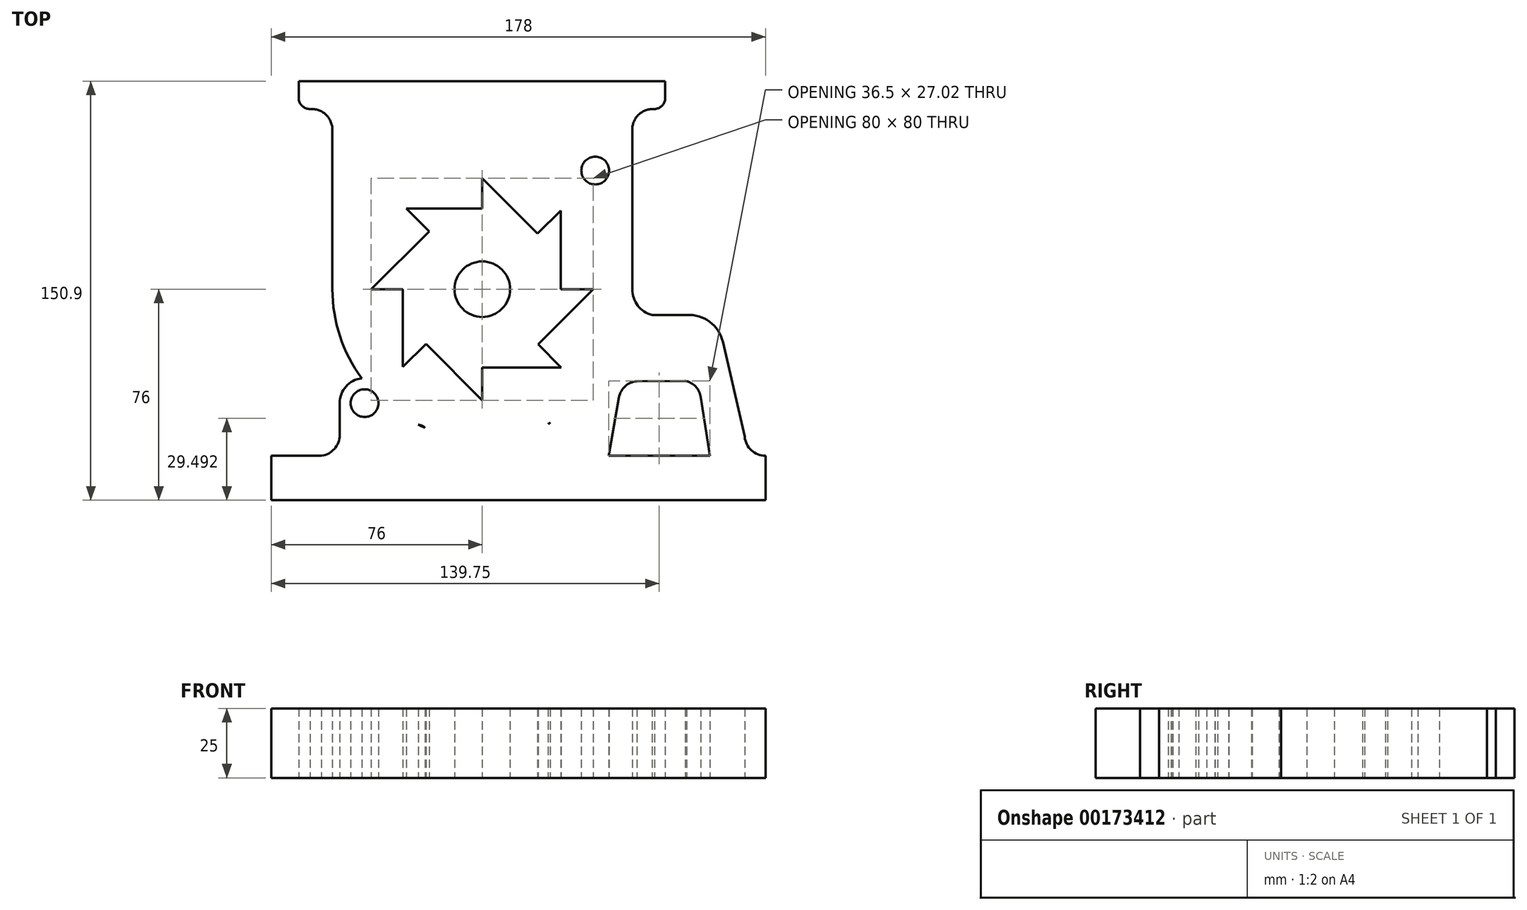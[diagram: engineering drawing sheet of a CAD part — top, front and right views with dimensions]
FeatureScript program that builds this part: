
annotation { "Feature Type Name" : "Feature", "Feature Type Description" : "" }
export const myFeature = defineFeature(function(context is Context, id is Id, definition is map)
    precondition{}
    {
        {
            var Q0;
            Q0=qCreatedBy(makeId("Top.planeOp"),FACE);
            var sketch = newSketch(context, id + "F0", { "sketchPlane" : qUnion([Q0])});
            skCircle(sketch, "E0", {"center": v(0, 0) * mm, "radius": 10 * mm});
            skCircle(sketch, "E1", {"center": v(0, 0) * mm, "radius": 45 * mm});
            skArc(sketch, "E2", {"start": v(-33.49, -42.36) * mm, "mid": v(38.34, -38.02) * mm, "end": v(42.08, 33.84) * mm});
            skLineSegment(sketch, "E3", {"start": v(0, 10) * mm, "end": v(0, 40) * mm});
            skLineSegment(sketch, "E4", {"start": v(10, 0) * mm, "end": v(40, 0) * mm});
            skLineSegment(sketch, "E5", {"start": v(0, -10) * mm, "end": v(0, -40) * mm});
            skLineSegment(sketch, "E6", {"start": v(-10, 0) * mm, "end": v(-40, 0) * mm});
            skLineSegment(sketch, "E7", {"start": v(7, 7.14) * mm, "end": v(28.22, 28.35) * mm});
            skLineSegment(sketch, "E8", {"start": v(7.18, -6.96) * mm, "end": v(28.4, -28.17) * mm});
            skLineSegment(sketch, "E9", {"start": v(-7.37, -6.76) * mm, "end": v(-28.58, -27.98) * mm});
            skLineSegment(sketch, "E10", {"start": v(-6.19, 7.86) * mm, "end": v(-27.4, 29.07) * mm});
            skLineSegment(sketch, "E11", {"start": v(-27.4, 29.07) * mm, "end": v(0, 29.07) * mm});
            skLineSegment(sketch, "E12", {"start": v(28.22, 28.35) * mm, "end": v(28.22, 0) * mm});
            skLineSegment(sketch, "E13", {"start": v(28.4, -28.17) * mm, "end": v(0, -28.17) * mm});
            skPoint(sketch, "E13.endSnap0", {"position": v(0, -25) * mm});
            skLineSegment(sketch, "E14", {"start": v(-28.58, -27.98) * mm, "end": v(-28.58, 0) * mm});
            skLineSegment(sketch, "E15", {"start": v(-40, 0) * mm, "end": v(-19.16, 20.84) * mm});
            skLineSegment(sketch, "E16", {"start": v(0, 40) * mm, "end": v(19.94, 20.06) * mm});
            skLineSegment(sketch, "E17", {"start": v(40, 0) * mm, "end": v(20.11, -19.89) * mm});
            skLineSegment(sketch, "E18", {"start": v(0, -40) * mm, "end": v(-20.3, -19.7) * mm});
            skLineSegment(sketch, "E19", {"start": v(-54, 0) * mm, "end": v(-54, 57.42) * mm});
            skLineSegment(sketch, "E20", {"start": v(54, 0) * mm, "end": v(54, 57.42) * mm});
            skArc(sketch, "E21", {"start": v(62.07, 64.9) * mm, "mid": v(56.4, 62.93) * mm, "end": v(54, 57.42) * mm});
            skArc(sketch, "E22", {"start": v(-54, 57.42) * mm, "mid": v(-56.4, 62.93) * mm, "end": v(-62.07, 64.9) * mm});
            skArc(sketch, "E23", {"start": v(-66.06, 68.05) * mm, "mid": v(-64.63, 65.76) * mm, "end": v(-62.07, 64.9) * mm});
            skArc(sketch, "E24", {"start": v(62.07, 64.9) * mm, "mid": v(64.5, 65.83) * mm, "end": v(65.84, 68.05) * mm});
            skLineSegment(sketch, "E25", {"start": v(65.84, 68.05) * mm, "end": v(65.84, 74.9) * mm});
            skLineSegment(sketch, "E26", {"start": v(65.84, 74.9) * mm, "end": v(-66.06, 74.9) * mm});
            skLineSegment(sketch, "E27", {"start": v(-66.06, 74.9) * mm, "end": v(-66.06, 68.05) * mm});
            skLineSegment(sketch, "E28", {"start": v(-62.07, 64.9) * mm, "end": v(62.07, 64.9) * mm});
            skLineSegment(sketch, "E29", {"start": v(-76, -76) * mm, "end": v(-76, -59.99) * mm});
            skLineSegment(sketch, "E30", {"start": v(0, -76) * mm, "end": v(102, -76) * mm});
            skLineSegment(sketch, "E31", {"start": v(102, -76) * mm, "end": v(102, -60.02) * mm});
            skCircle(sketch, "E32", {"center": v(-42.39, -41.04) * mm, "radius": 5 * mm});
            skArc(sketch, "E33", {"start": v(-43.42, -32.1) * mm, "mid": v(-48.85, -47.3) * mm, "end": v(-33.49, -42.36) * mm});
            skLineSegment(sketch, "E34", {"start": v(-51.39, -41.04) * mm, "end": v(-51.39, -52.55) * mm});
            skArc(sketch, "E35", {"start": v(-57.95, -59.99) * mm, "mid": v(-53.26, -57.5) * mm, "end": v(-51.39, -52.55) * mm});
            skLineSegment(sketch, "E36", {"start": v(-76, -59.99) * mm, "end": v(-23.03, -59.99) * mm});
            skArc(sketch, "E37", {"start": v(-23.03, -59.99) * mm, "mid": v(-20.87, -59.36) * mm, "end": v(-19.4, -57.66) * mm});
            skArc(sketch, "E38", {"start": v(-19.4, -53.45) * mm, "mid": v(-20.2, -50.35) * mm, "end": v(-23.03, -48.84) * mm});
            skLineSegment(sketch, "E39", {"start": v(-19.4, -53.45) * mm, "end": v(-19.4, -57.66) * mm});
            skLineSegment(sketch, "E40", {"start": v(-76, -76) * mm, "end": v(0, -76) * mm});
            skLineSegment(sketch, "E41", {"start": v(102, -60.02) * mm, "end": v(23.1, -60.02) * mm});
            skArc(sketch, "E42", {"start": v(20, -57.43) * mm, "mid": v(21.08, -59.29) * mm, "end": v(23.1, -60.02) * mm});
            skLineSegment(sketch, "E43", {"start": v(20, -57.43) * mm, "end": v(20, -54.9) * mm});
            skArc(sketch, "E44", {"start": v(24.4, -48.17) * mm, "mid": v(21.2, -50.88) * mm, "end": v(20, -54.9) * mm});
            skCircle(sketch, "E45", {"center": v(40.68, 42.73) * mm, "radius": 5 * mm});
            skArc(sketch, "E46", {"start": v(42.08, 33.84) * mm, "mid": v(46.89, 49.25) * mm, "end": v(31.73, 43.7) * mm});
            skArc(sketch, "E47.trimOffspring", {"start": v(31.73, 43.7) * mm, "mid": v(-38.34, 38.02) * mm, "end": v(-43.42, -32.1) * mm});
            skLineSegment(sketch, "E48", {"start": v(45.5, -60.02) * mm, "end": v(49.27, -38.92) * mm});
            skArc(sketch, "E49", {"start": v(55.7, -33.16) * mm, "mid": v(51.49, -34.93) * mm, "end": v(49.27, -38.92) * mm});
            skArc(sketch, "E50", {"start": v(78.67, -38.92) * mm, "mid": v(76.85, -35.08) * mm, "end": v(73.14, -33) * mm});
            skLineSegment(sketch, "E51", {"start": v(78.67, -38.92) * mm, "end": v(82, -60.02) * mm});
            skLineSegment(sketch, "E52", {"start": v(55.7, -33.16) * mm, "end": v(73.14, -33) * mm});
            skArc(sketch, "E53", {"start": v(94.53, -53.17) * mm, "mid": v(96.93, -58.05) * mm, "end": v(102, -60.02) * mm});
            skLineSegment(sketch, "E54", {"start": v(94.53, -53.17) * mm, "end": v(86.66, -18.98) * mm});
            skArc(sketch, "E55", {"start": v(86.66, -18.98) * mm, "mid": v(81.91, -11.74) * mm, "end": v(73.59, -9.32) * mm});
            skLineSegment(sketch, "E56", {"start": v(73.59, -9.32) * mm, "end": v(61.13, -9.32) * mm});
            skArc(sketch, "E57", {"start": v(54, 0) * mm, "mid": v(55.99, -5.87) * mm, "end": v(61.13, -9.32) * mm});
            skSolve(sketch);
        }
        {
            var Q0;
            {var subQ1=sQuery(id+"F0.wireOp",EDGE,"E23");Q0=makeQuery(id+"F0.imprint","IMPRINT",FACE,{"disambiguationData":[TD([[makeQuery(id+"F0.imprint","IMPRINT",EDGE,{"derivedFrom":subQ1}),1.0]])]});}
            var Q1;
            {var subQ1=sQuery(id+"F0.wireOp",EDGE,"E19");Q1=makeQuery(id+"F0.imprint","IMPRINT",FACE,{"disambiguationData":[TD([[makeQuery(id+"F0.imprint","IMPRINT",EDGE,{"derivedFrom":subQ1}),-1.0]])]});}
            var Q2;
            Q2=makeQuery(id+"F0.imprint","IMPRINT",FACE,{"disambiguationData":[TD([[makeQuery(id+"F0.imprint","IMPRINT",EDGE,{"derivedFrom":sQuery(id+"F0.wireOp",EDGE,"E1")}),-1.0]])]});
            var Q3;
            Q3=makeQuery(id+"F0.imprint","IMPRINT",FACE,{"disambiguationData":[TD([[makeQuery(id+"F0.imprint","IMPRINT",EDGE,{"derivedFrom":sQuery(id+"F0.wireOp",EDGE,"E1")}),1.0]])]});
            var Q4;
            {var subQ0=sQuery(id+"F0.wireOp",EDGE,"E0");var subQ5=makeQuery(id+"F0.imprint","INTERSECT",VERTEX,{"derivedFrom":[subQ0,sQuery(id+"F0.wireOp",EDGE,"E4")]});Q4=makeQuery(id+"F0.imprint","IMPRINT",FACE,{"disambiguationData":[TD([[makeQuery(id+"F0.imprint","IMPRINT",EDGE,{"disambiguationData":[TD([[subQ5,-1.0]])],"derivedFrom":subQ0}),1.0]])]});}
            var Q5;
            {var subQ0=sQuery(id+"F0.wireOp",EDGE,"E34");Q5=makeQuery(id+"F0.imprint","IMPRINT",FACE,{"disambiguationData":[TD([[makeQuery(id+"F0.imprint","IMPRINT",EDGE,{"derivedFrom":subQ0}),1.0]])]});}
            var Q6;
            {var subQ9=sQuery(id+"F0.wireOp",EDGE,"E29");Q6=makeQuery(id+"F0.imprint","IMPRINT",FACE,{"disambiguationData":[TD([[makeQuery(id+"F0.imprint","IMPRINT",EDGE,{"derivedFrom":subQ9}),-1.0]])]});}
            var Q7;
            {var subQ7=sQuery(id+"F0.wireOp",EDGE,"E42");Q7=makeQuery(id+"F0.imprint","IMPRINT",FACE,{"disambiguationData":[TD([[makeQuery(id+"F0.imprint","IMPRINT",EDGE,{"derivedFrom":subQ7}),1.0]])]});}
            extrude(context, id + "F1", {"entities" : qUnion([Q0, Q1, Q2, Q3, Q4, Q5, Q6, Q7]), "depth" : 25 * mm});
        }
    });
